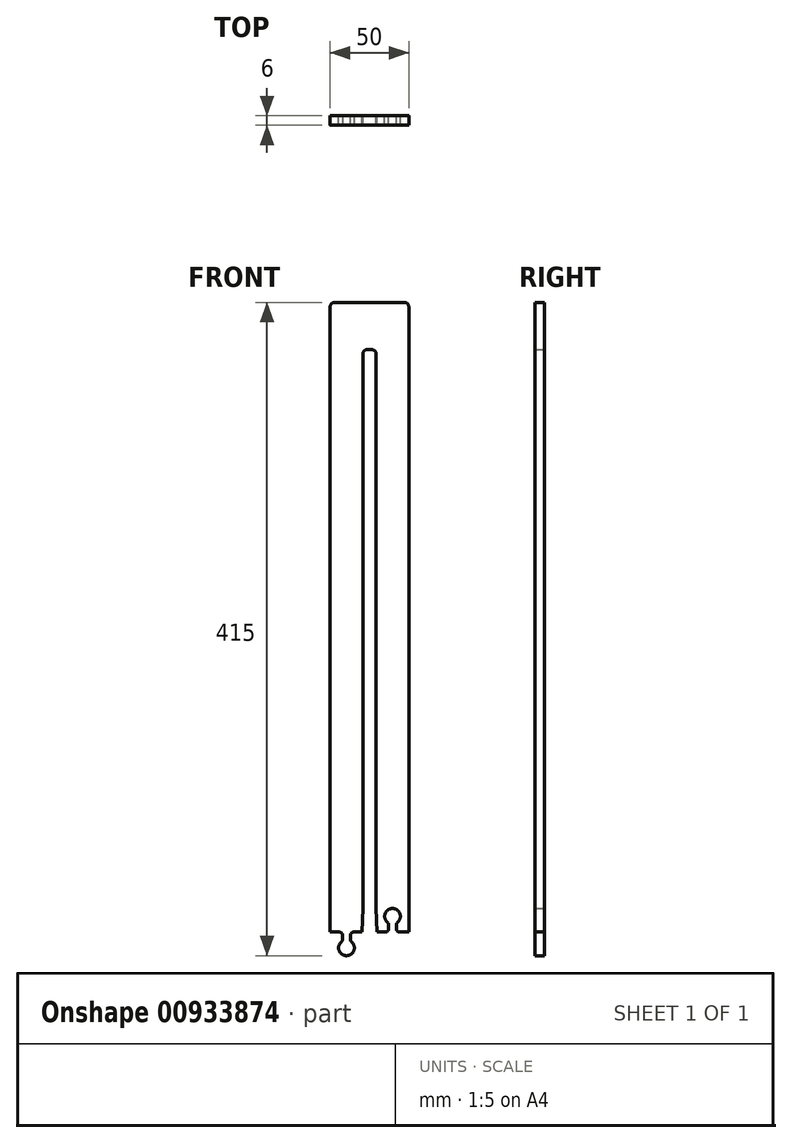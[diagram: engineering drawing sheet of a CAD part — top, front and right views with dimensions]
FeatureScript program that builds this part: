
annotation { "Feature Type Name" : "Feature", "Feature Type Description" : "" }
export const myFeature = defineFeature(function(context is Context, id is Id, definition is map)
    precondition{}
    {
        {
            var Q0;
            Q0=qCreatedBy(makeId("Front.planeOp"),FACE);
            var sketch = newSketch(context, id + "F0", { "sketchPlane" : qUnion([Q0])});
            skLineSegment(sketch, "E0.bottom", {"start": v(0, 0) * mm, "end": v(-50, 0) * mm});
            skLineSegment(sketch, "E0.left", {"start": v(0, 0) * mm, "end": v(0, -400) * mm});
            skLineSegment(sketch, "E0.right", {"start": v(-50, 0) * mm, "end": v(-50, -400) * mm});
            skLineSegment(sketch, "E1.top", {"start": v(-20.75, -30) * mm, "end": v(-29.25, -30) * mm});
            skLineSegment(sketch, "E1.left", {"start": v(-20.75, -400) * mm, "end": v(-20.75, -385) * mm, "construction": true});
            skLineSegment(sketch, "E1.right", {"start": v(-29.25, -400) * mm, "end": v(-29.25, -385) * mm, "construction": true});
            skLineSegment(sketch, "E2", {"start": v(-25, -30) * mm, "end": v(-25, 0) * mm, "construction": true});
            skLineSegment(sketch, "E3.trimOffspring", {"start": v(-29.25, -400) * mm, "end": v(-29.75, -400) * mm, "construction": true});
            skArc(sketch, "E4", {"start": v(-7.87, -394.33) * mm, "mid": v(-10.37, -385) * mm, "end": v(-12.88, -394.33) * mm});
            skLineSegment(sketch, "E5", {"start": v(-10.37, -390) * mm, "end": v(-10.37, -400) * mm, "construction": true});
            skPoint(sketch, "E6.visualSharp", {"position": v(0, 0) * mm});
            skPoint(sketch, "E7.visualSharp", {"position": v(-50, 0) * mm});
            skPoint(sketch, "E8.visualSharp", {"position": v(-29.25, -30) * mm});
            skPoint(sketch, "E9.visualSharp", {"position": v(-20.75, -30) * mm});
            skLineSegment(sketch, "E10", {"start": v(-20.75, -385) * mm, "end": v(-20.25, -400) * mm});
            skLineSegment(sketch, "E11", {"start": v(-29.75, -400) * mm, "end": v(-29.25, -385) * mm});
            skLineSegment(sketch, "E12", {"start": v(-20.75, -385) * mm, "end": v(-29.25, -385) * mm, "construction": true});
            skLineSegment(sketch, "E13", {"start": v(-7.87, -400) * mm, "end": v(-7.87, -394.33) * mm});
            skLineSegment(sketch, "E14", {"start": v(-12.87, -400) * mm, "end": v(-12.87, -394.33) * mm});
            skLineSegment(sketch, "E15", {"start": v(-39.63, -400) * mm, "end": v(-39.63, -410) * mm, "construction": true});
            skArc(sketch, "E16", {"start": v(-42.12, -405.67) * mm, "mid": v(-39.62, -415) * mm, "end": v(-37.13, -405.67) * mm});
            skLineSegment(sketch, "E17", {"start": v(-37.12, -400) * mm, "end": v(-37.12, -405.67) * mm});
            skLineSegment(sketch, "E18", {"start": v(-42.12, -400) * mm, "end": v(-42.12, -405.67) * mm});
            skLineSegment(sketch, "E19.trimOffspring", {"start": v(-37.12, -400) * mm, "end": v(-42.12, -400) * mm, "construction": true});
            skLineSegment(sketch, "E20", {"start": v(-50, -400) * mm, "end": v(-42.12, -400) * mm});
            skLineSegment(sketch, "E21", {"start": v(-37.12, -400) * mm, "end": v(-29.75, -400) * mm});
            skLineSegment(sketch, "E22", {"start": v(-20.75, -400) * mm, "end": v(-20.25, -400) * mm, "construction": true});
            skLineSegment(sketch, "E23", {"start": v(-20.25, -400) * mm, "end": v(-12.87, -400) * mm});
            skLineSegment(sketch, "E24", {"start": v(-12.87, -400) * mm, "end": v(-7.87, -400) * mm, "construction": true});
            skLineSegment(sketch, "E25", {"start": v(-7.87, -400) * mm, "end": v(0, -400) * mm});
            skLineSegment(sketch, "E26", {"start": v(-20.75, -30) * mm, "end": v(-20.75, -385) * mm});
            skLineSegment(sketch, "E27", {"start": v(-29.25, -385) * mm, "end": v(-29.25, -30) * mm});
            skSolve(sketch);
        }
        {
            assignVariable(context, id + "F1", {"name" : "RadiusLock", "anyValue" : 2});
        }
        {
            assignVariable(context, id + "F2", {"name" : "RadiusCorner", "anyValue" : 3});
        }
        {
            var Q0;
            Q0 = qSketchRegion(id + "F0", true);
            extrude(context, id + "F3", {"entities" : qUnion([Q0]), "endBound" : BoundingType.SYMMETRIC, "depth" : 6 * mm, "offsetDistance" : 25 * mm});
        }
        {
            var Q0;
            Q0=makeQuery(id+"F3.opExtrude","SWEPT_EDGE",EDGE,{"disambiguationData":[OSD([sQuery(id+"F0.wireOp",EDGE,"E0.bottom"),sQuery(id+"F0.wireOp",EDGE,"E0.right")])]});
            var Q1;
            Q1=makeQuery(id+"F3.opExtrude","SWEPT_EDGE",EDGE,{"disambiguationData":[OSD([sQuery(id+"F0.wireOp",EDGE,"E0.bottom"),sQuery(id+"F0.wireOp",EDGE,"E0.left")])]});
            var Q2;
            Q2=makeQuery(id+"F3.opExtrude","SWEPT_EDGE",EDGE,{"disambiguationData":[OSD([sQuery(id+"F0.wireOp",EDGE,"E1.top"),sQuery(id+"F0.wireOp",EDGE,"E26")])]});
            var Q3;
            Q3=makeQuery(id+"F3.opExtrude","SWEPT_EDGE",EDGE,{"disambiguationData":[OSD([sQuery(id+"F0.wireOp",EDGE,"E1.top"),sQuery(id+"F0.wireOp",EDGE,"E27")])]});
            fillet(context, id + "F4", {"entities" : qUnion([Q0, Q1, Q2, Q3]), "radius" : (getVariable(context, 'RadiusCorner')) * mm, "tangentPropagation" : true, "allowEdgeOverflow" : false});
        }
        {
            var Q0;
            Q0=makeQuery(id+"F3.opExtrude","SWEPT_EDGE",EDGE,{"disambiguationData":[OSD([sQuery(id+"F0.wireOp",EDGE,"E4"),sQuery(id+"F0.wireOp",EDGE,"E14")])]});
            var Q1;
            Q1=makeQuery(id+"F3.opExtrude","SWEPT_EDGE",EDGE,{"disambiguationData":[OSD([sQuery(id+"F0.wireOp",EDGE,"E14"),sQuery(id+"F0.wireOp",EDGE,"E23")])]});
            var Q2;
            Q2=makeQuery(id+"F3.opExtrude","SWEPT_EDGE",EDGE,{"disambiguationData":[OSD([sQuery(id+"F0.wireOp",EDGE,"E17"),sQuery(id+"F0.wireOp",EDGE,"E21")])]});
            var Q3;
            Q3=makeQuery(id+"F3.opExtrude","SWEPT_EDGE",EDGE,{"disambiguationData":[OSD([sQuery(id+"F0.wireOp",EDGE,"E13"),sQuery(id+"F0.wireOp",EDGE,"E25")])]});
            var Q4;
            Q4=makeQuery(id+"F3.opExtrude","SWEPT_EDGE",EDGE,{"disambiguationData":[OSD([sQuery(id+"F0.wireOp",EDGE,"E4"),sQuery(id+"F0.wireOp",EDGE,"E13")])]});
            var Q5;
            Q5=makeQuery(id+"F3.opExtrude","SWEPT_EDGE",EDGE,{"disambiguationData":[OSD([sQuery(id+"F0.wireOp",EDGE,"E18"),sQuery(id+"F0.wireOp",EDGE,"E20")])]});
            var Q6;
            Q6=makeQuery(id+"F3.opExtrude","SWEPT_EDGE",EDGE,{"disambiguationData":[OSD([sQuery(id+"F0.wireOp",EDGE,"E16"),sQuery(id+"F0.wireOp",EDGE,"E18")])]});
            var Q7;
            Q7=makeQuery(id+"F3.opExtrude","SWEPT_EDGE",EDGE,{"disambiguationData":[OSD([sQuery(id+"F0.wireOp",EDGE,"E16"),sQuery(id+"F0.wireOp",EDGE,"E17")])]});
            fillet(context, id + "F5", {"entities" : qUnion([Q0, Q1, Q2, Q3, Q4, Q5, Q6, Q7]), "radius" : (getVariable(context, 'RadiusLock')) * mm, "tangentPropagation" : true, "allowEdgeOverflow" : false});
        }
    });
